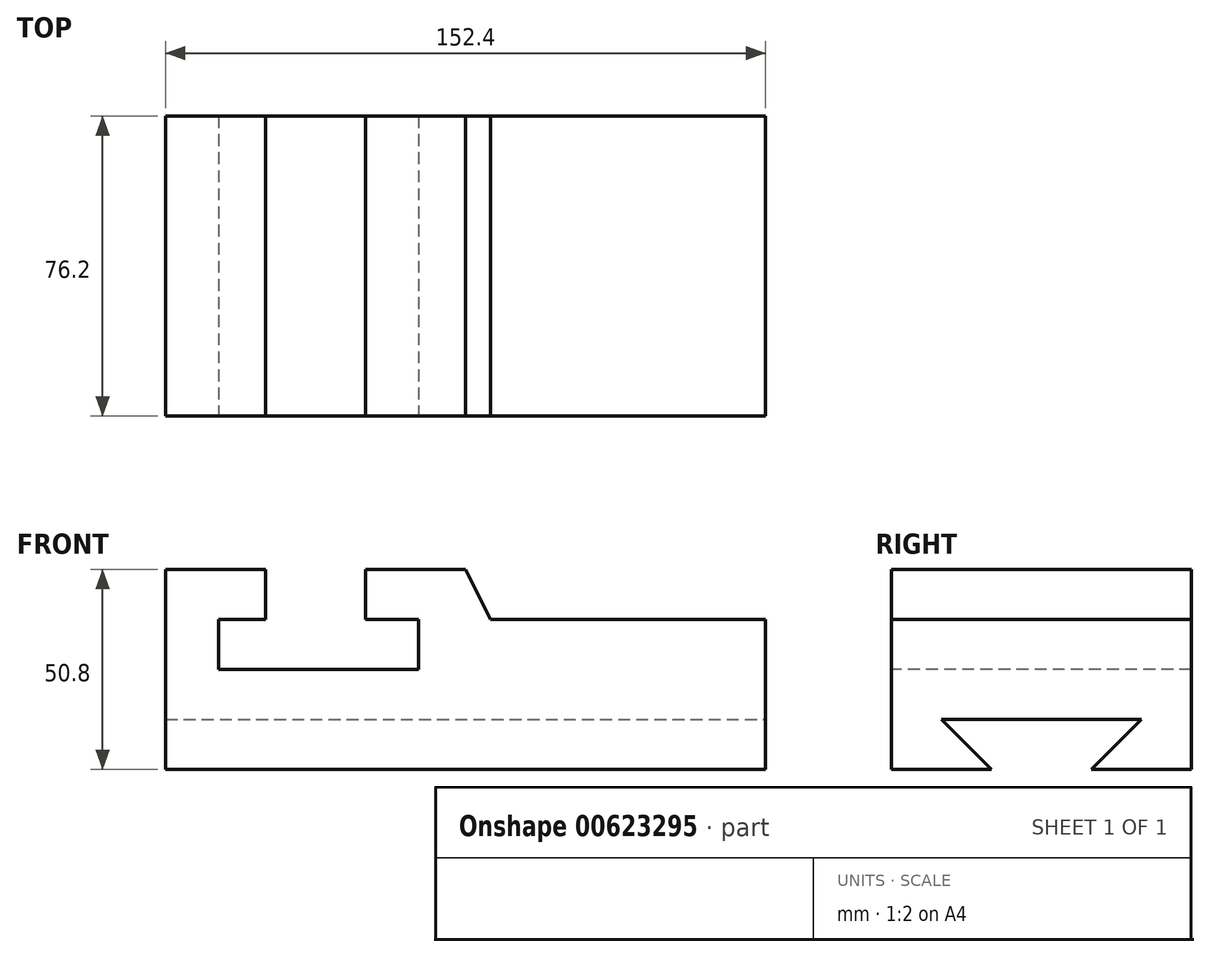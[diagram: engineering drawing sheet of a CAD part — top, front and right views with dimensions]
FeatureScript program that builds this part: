
annotation { "Feature Type Name" : "Feature", "Feature Type Description" : "" }
export const myFeature = defineFeature(function(context is Context, id is Id, definition is map)
    precondition{}
    {
        {
            var Q0;
            Q0=qCreatedBy(makeId("Front.planeOp"),FACE);
            var sketch = newSketch(context, id + "F0", { "sketchPlane" : qUnion([Q0])});
            skLineSegment(sketch, "E0", {"start": v(0, 0) * mm, "end": v(0, 50.8) * mm});
            skLineSegment(sketch, "E1", {"start": v(0, 50.8) * mm, "end": v(25.4, 50.8) * mm});
            skLineSegment(sketch, "E2", {"start": v(25.4, 50.8) * mm, "end": v(25.4, 38.1) * mm});
            skLineSegment(sketch, "E3", {"start": v(25.4, 38.1) * mm, "end": v(13.4, 38.1) * mm});
            skLineSegment(sketch, "E4", {"start": v(13.4, 38.1) * mm, "end": v(13.4, 25.4) * mm});
            skLineSegment(sketch, "E5", {"start": v(13.4, 25.4) * mm, "end": v(64.2, 25.4) * mm});
            skLineSegment(sketch, "E6", {"start": v(64.2, 25.4) * mm, "end": v(64.2, 38.1) * mm});
            skLineSegment(sketch, "E7", {"start": v(64.2, 38.1) * mm, "end": v(50.8, 38.1) * mm});
            skLineSegment(sketch, "E8", {"start": v(50.8, 38.1) * mm, "end": v(50.8, 50.8) * mm});
            skLineSegment(sketch, "E9", {"start": v(50.8, 50.8) * mm, "end": v(76.2, 50.8) * mm});
            skLineSegment(sketch, "E10", {"start": v(76.2, 50.8) * mm, "end": v(82.55, 38.1) * mm});
            skLineSegment(sketch, "E11", {"start": v(82.55, 38.1) * mm, "end": v(152.4, 38.1) * mm});
            skLineSegment(sketch, "E12", {"start": v(152.4, 38.1) * mm, "end": v(152.4, 0) * mm});
            skLineSegment(sketch, "E13", {"start": v(152.4, 0) * mm, "end": v(0, 0) * mm});
            skSolve(sketch);
        }
        {
            var Q0;
            Q0=makeQuery(id+"F0.imprint","IMPRINT",FACE,{"disambiguationData":[TD([[makeQuery(id+"F0.imprint","IMPRINT",EDGE,{"derivedFrom":sQuery(id+"F0.wireOp",EDGE,"E0")}),-1.0]])]});
            extrude(context, id + "F1", {"entities" : qUnion([Q0]), "oppositeDirection" : true, "depth" : 76.2 * mm, "offsetDistance" : 25.4 * mm});
        }
        {
            var Q0;
            Q0=makeQuery(id+"F1.opExtrude","SWEPT_FACE",FACE,{"disambiguationData":[OSD([sQuery(id+"F0.wireOp",EDGE,"E12")])]});
            var sketch = newSketch(context, id + "F2", { "sketchPlane" : qUnion([Q0])});
            skLineSegment(sketch, "E14", {"start": v(25.4, 0) * mm, "end": v(12.7, 12.7) * mm});
            skLineSegment(sketch, "E15", {"start": v(12.7, 12.7) * mm, "end": v(63.5, 12.7) * mm});
            skLineSegment(sketch, "E16", {"start": v(63.5, 12.7) * mm, "end": v(50.8, 0) * mm});
            skLineSegment(sketch, "E17", {"start": v(50.8, 0) * mm, "end": v(25.4, 0) * mm});
            skSolve(sketch);
        }
        {
            var Q0;
            Q0=makeQuery(id+"F2.imprint","IMPRINT",FACE,{"disambiguationData":[TD([[makeQuery(id+"F2.imprint","IMPRINT",EDGE,{"derivedFrom":sQuery(id+"F2.wireOp",EDGE,"E14")}),-1.0]])]});
            extrude(context, id + "F3", {"entities" : qUnion([Q0]), "operationType" : NewBodyOperationType.REMOVE, "oppositeDirection" : true, "depth" : 152.4 * mm, "offsetDistance" : 25.4 * mm});
        }
    });
